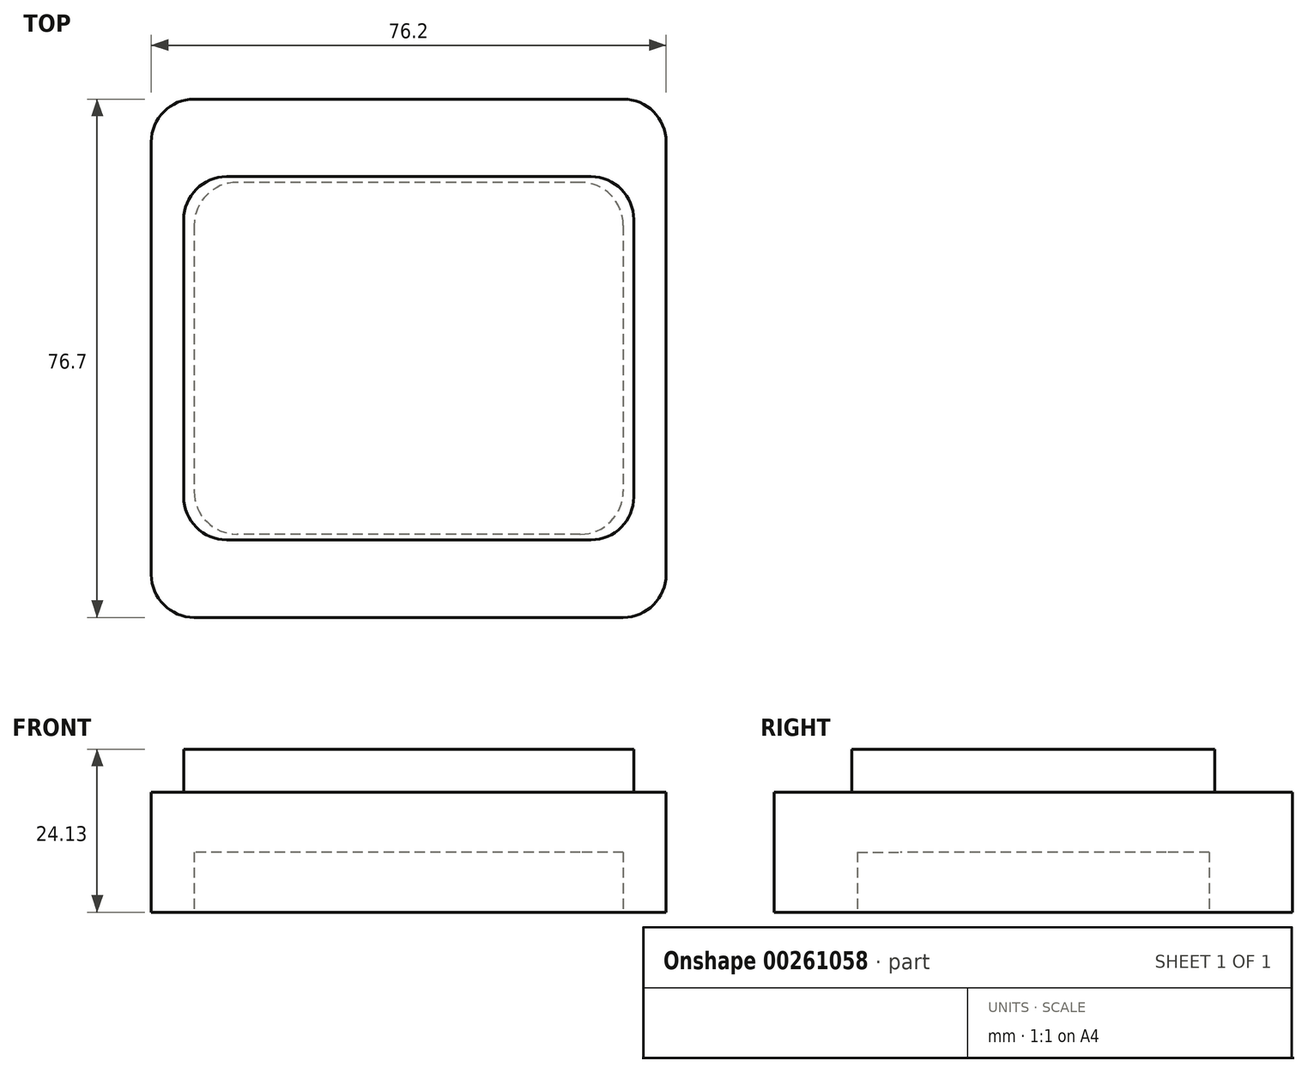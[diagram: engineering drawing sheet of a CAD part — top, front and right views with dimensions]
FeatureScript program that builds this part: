
annotation { "Feature Type Name" : "Feature", "Feature Type Description" : "" }
export const myFeature = defineFeature(function(context is Context, id is Id, definition is map)
    precondition{}
    {
        {
            var Q0;
            Q0=qCreatedBy(makeId("Top.planeOp"),FACE);
            var sketch = newSketch(context, id + "F0", { "sketchPlane" : qUnion([Q0])});
            skLineSegment(sketch, "E0.bottom", {"start": v(31.75, 38.35) * mm, "end": v(-31.75, 38.35) * mm});
            skLineSegment(sketch, "E0.top", {"start": v(31.75, -38.35) * mm, "end": v(-31.75, -38.35) * mm});
            skLineSegment(sketch, "E0.left", {"start": v(38.1, 32) * mm, "end": v(38.1, -32) * mm});
            skLineSegment(sketch, "E0.right", {"start": v(-38.1, 32) * mm, "end": v(-38.1, -32) * mm});
            skPoint(sketch, "E0.middle", {"position": v(0, 0) * mm});
            skLineSegment(sketch, "E1.bottom", {"start": v(25.4, 26.04) * mm, "end": v(-25.4, 26.04) * mm});
            skLineSegment(sketch, "E1.top", {"start": v(25.4, -26.04) * mm, "end": v(-25.4, -26.04) * mm});
            skLineSegment(sketch, "E1.left", {"start": v(31.75, 19.69) * mm, "end": v(31.75, -19.69) * mm});
            skLineSegment(sketch, "E1.right", {"start": v(-31.75, 19.69) * mm, "end": v(-31.75, -19.69) * mm});
            skPoint(sketch, "E2.visualSharp", {"position": v(-38.1, 38.35) * mm});
            skArc(sketch, "E2.filletArc", {"start": v(-31.75, 38.35) * mm, "mid": v(-36.24, 36.5) * mm, "end": v(-38.1, 32) * mm});
            skPoint(sketch, "E3.visualSharp", {"position": v(38.1, 38.35) * mm});
            skArc(sketch, "E3.filletArc", {"start": v(38.1, 32) * mm, "mid": v(36.24, 36.5) * mm, "end": v(31.75, 38.35) * mm});
            skPoint(sketch, "E4.visualSharp", {"position": v(38.1, -38.35) * mm});
            skArc(sketch, "E4.filletArc", {"start": v(31.75, -38.35) * mm, "mid": v(36.24, -36.5) * mm, "end": v(38.1, -32) * mm});
            skPoint(sketch, "E5.visualSharp", {"position": v(-38.1, -38.35) * mm});
            skArc(sketch, "E5.filletArc", {"start": v(-38.1, -32) * mm, "mid": v(-36.24, -36.5) * mm, "end": v(-31.75, -38.35) * mm});
            skPoint(sketch, "E6.visualSharp", {"position": v(31.75, 26.04) * mm});
            skArc(sketch, "E6.filletArc", {"start": v(31.75, 19.69) * mm, "mid": v(29.9, 24.18) * mm, "end": v(25.4, 26.04) * mm});
            skPoint(sketch, "E7.visualSharp", {"position": v(-31.75, 26.04) * mm});
            skArc(sketch, "E7.filletArc", {"start": v(-25.4, 26.04) * mm, "mid": v(-29.9, 24.18) * mm, "end": v(-31.75, 19.69) * mm});
            skPoint(sketch, "E8.visualSharp", {"position": v(-31.75, -26.04) * mm});
            skArc(sketch, "E8.filletArc", {"start": v(-31.75, -19.69) * mm, "mid": v(-29.9, -24.18) * mm, "end": v(-25.4, -26.04) * mm});
            skPoint(sketch, "E9.visualSharp", {"position": v(31.75, -26.04) * mm});
            skArc(sketch, "E9.filletArc", {"start": v(25.4, -26.04) * mm, "mid": v(29.9, -24.18) * mm, "end": v(31.75, -19.69) * mm});
            skSolve(sketch);
        }
        {
            var Q0;
            Q0 = qSketchRegion(id + "F0", true);
            extrude(context, id + "F1", {"entities" : qUnion([Q0]), "endBound" : BoundingType.SYMMETRIC, "depth" : 17.78 * mm});
        }
        {
            var Q0;
            Q0=qCreatedBy(makeId("Top.planeOp"),FACE);
            var sketch = newSketch(context, id + "F2", { "sketchPlane" : qUnion([Q0])});
            skLineSegment(sketch, "E10.bottom", {"start": v(26.96, 26.87) * mm, "end": v(-26.96, 26.87) * mm});
            skLineSegment(sketch, "E10.top", {"start": v(26.96, -26.87) * mm, "end": v(-26.96, -26.87) * mm});
            skLineSegment(sketch, "E10.left", {"start": v(33.31, 20.52) * mm, "end": v(33.31, -20.52) * mm});
            skLineSegment(sketch, "E10.right", {"start": v(-33.31, 20.52) * mm, "end": v(-33.31, -20.52) * mm});
            skPoint(sketch, "E10.middle", {"position": v(0, 0) * mm});
            skPoint(sketch, "E11.visualSharp", {"position": v(33.31, 26.87) * mm});
            skArc(sketch, "E11.filletArc", {"start": v(33.31, 20.52) * mm, "mid": v(31.45, 25) * mm, "end": v(26.96, 26.87) * mm});
            skPoint(sketch, "E12.visualSharp", {"position": v(33.31, -26.87) * mm});
            skArc(sketch, "E12.filletArc", {"start": v(26.96, -26.87) * mm, "mid": v(31.45, -25) * mm, "end": v(33.31, -20.52) * mm});
            skPoint(sketch, "E13.visualSharp", {"position": v(-33.31, -26.87) * mm});
            skArc(sketch, "E13.filletArc", {"start": v(-33.31, -20.52) * mm, "mid": v(-31.45, -25) * mm, "end": v(-26.96, -26.87) * mm});
            skPoint(sketch, "E14.visualSharp", {"position": v(-33.31, 26.87) * mm});
            skArc(sketch, "E14.filletArc", {"start": v(-26.96, 26.87) * mm, "mid": v(-31.45, 25) * mm, "end": v(-33.31, 20.52) * mm});
            skSolve(sketch);
        }
        {
            var Q0;
            Q0 = qSketchRegion(id + "F2", true);
            extrude(context, id + "F3", {"entities" : qUnion([Q0]), "operationType" : NewBodyOperationType.ADD, "depth" : 15.24 * mm});
        }
    });
